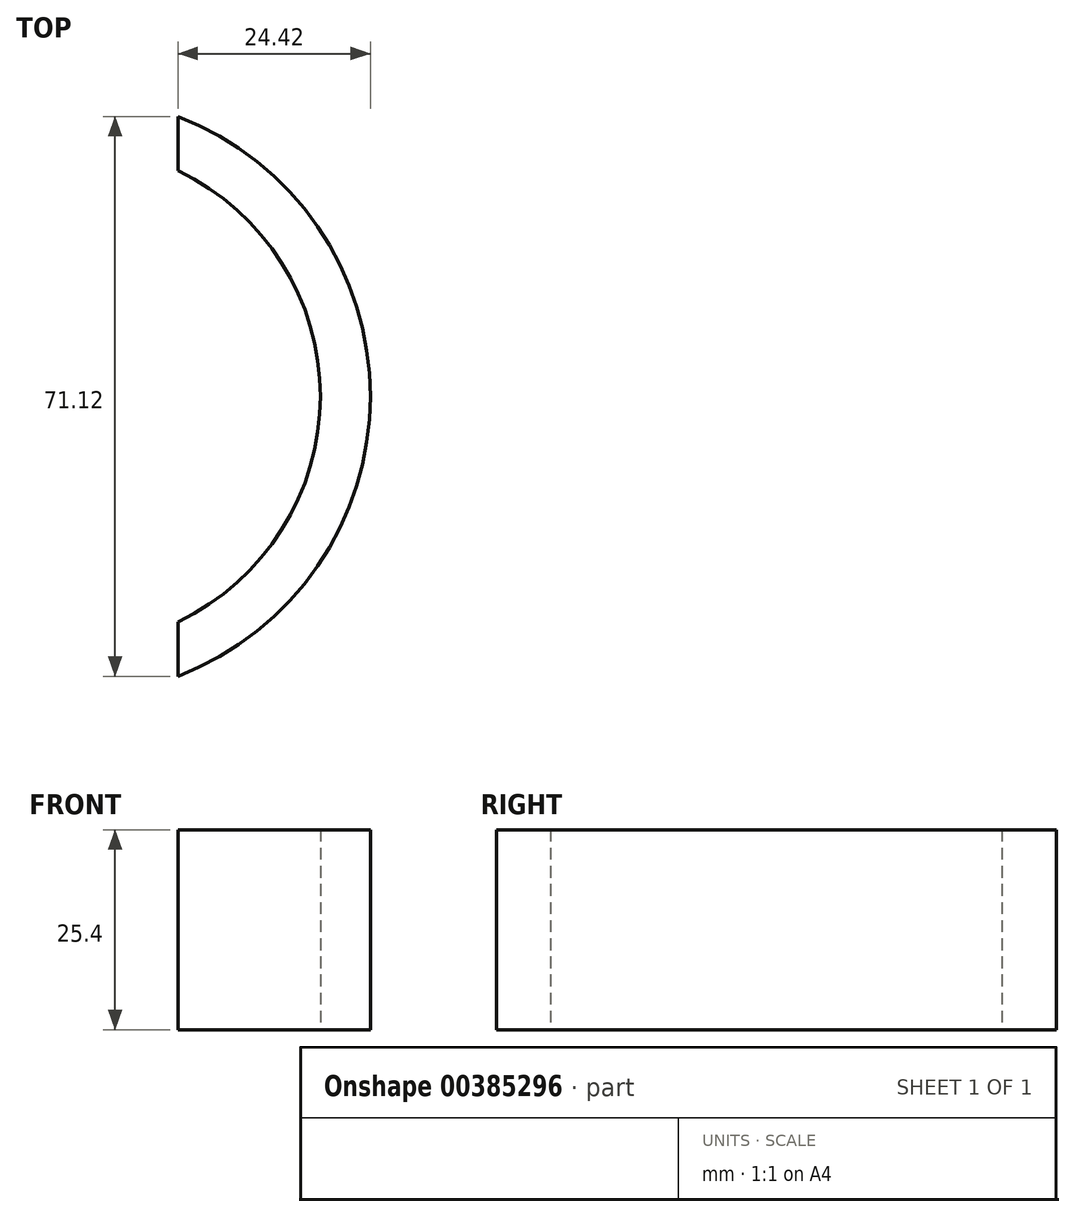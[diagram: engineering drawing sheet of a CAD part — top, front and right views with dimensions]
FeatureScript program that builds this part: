
annotation { "Feature Type Name" : "Feature", "Feature Type Description" : "" }
export const myFeature = defineFeature(function(context is Context, id is Id, definition is map)
    precondition{}
    {
        {
            var Q0;
            Q0=qCreatedBy(makeId("Top.planeOp"),FACE);
            var sketch = newSketch(context, id + "F0", { "sketchPlane" : qUnion([Q0])});
            skCircle(sketch, "E0", {"center": v(0, 0) * mm, "radius": 38.1 * mm});
            skCircle(sketch, "E1", {"center": v(0, 0) * mm, "radius": 31.75 * mm});
            skLineSegment(sketch, "E2", {"start": v(13.68, -35.56) * mm, "end": v(13.68, 35.56) * mm});
            skSolve(sketch);
        }
        {
            var Q0;
            {var subQ0=sQuery(id+"F0.wireOp",EDGE,"E2");var subQ1=sQuery(id+"F0.wireOp",EDGE,"E0");var subQ2=makeQuery(id+"F0.imprint","INTERSECT",VERTEX,{"disambiguationData":[OD(0.0)],"derivedFrom":[subQ1,subQ0]});Q0=makeQuery(id+"F0.imprint","IMPRINT",FACE,{"disambiguationData":[TD([[makeQuery(id+"F0.imprint","IMPRINT",EDGE,{"disambiguationData":[TD([[subQ2,1.0]])],"derivedFrom":subQ1}),1.0]])]});}
            extrude(context, id + "F1", {"entities" : qUnion([Q0]), "depth" : 25.4 * mm});
        }
    });
